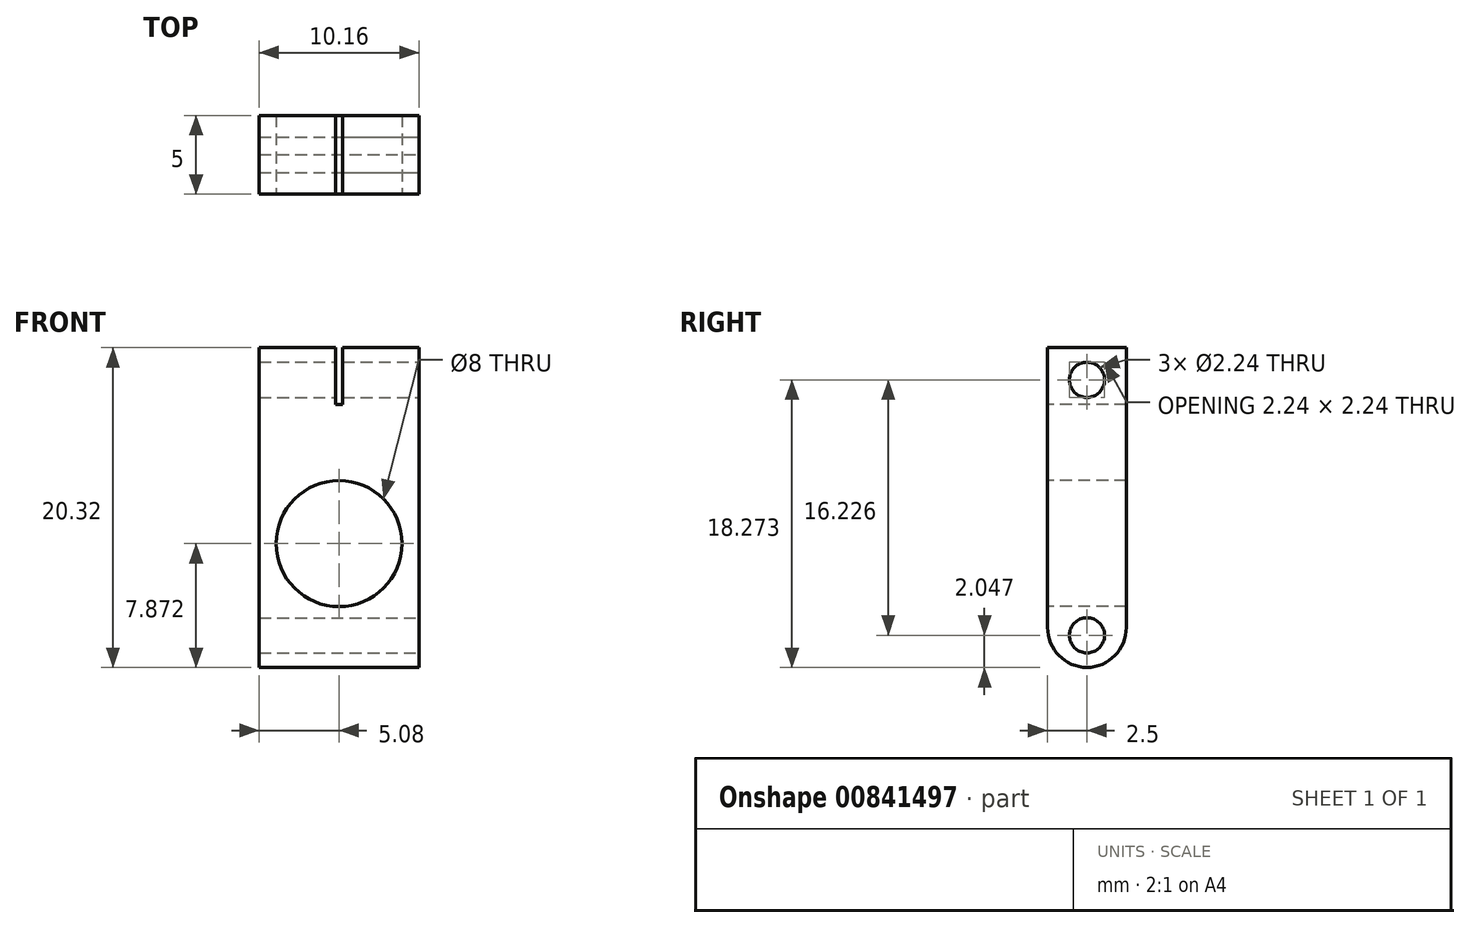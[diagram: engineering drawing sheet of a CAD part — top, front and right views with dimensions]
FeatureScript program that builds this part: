
annotation { "Feature Type Name" : "Feature", "Feature Type Description" : "" }
export const myFeature = defineFeature(function(context is Context, id is Id, definition is map)
    precondition{}
    {
        {
            var Q0;
            Q0=qCreatedBy(makeId("Front.planeOp"),FACE);
            var sketch = newSketch(context, id + "F0", { "sketchPlane" : qUnion([Q0])});
            skLineSegment(sketch, "E0.bottom", {"start": v(5.08, -10.16) * mm, "end": v(-5.08, -10.16) * mm});
            skLineSegment(sketch, "E0.top", {"start": v(5.08, 10.16) * mm, "end": v(-5.08, 10.16) * mm});
            skLineSegment(sketch, "E0.left", {"start": v(5.08, -10.16) * mm, "end": v(5.08, 10.16) * mm});
            skLineSegment(sketch, "E0.right", {"start": v(-5.08, -10.16) * mm, "end": v(-5.08, 10.16) * mm});
            skPoint(sketch, "E0.middle", {"position": v(0, 0) * mm});
            skSolve(sketch);
        }
        {
            var Q0;
            Q0=makeQuery(id+"F0.imprint","IMPRINT",FACE,{"disambiguationData":[TD([[makeQuery(id+"F0.imprint","IMPRINT",EDGE,{"derivedFrom":sQuery(id+"F0.wireOp",EDGE,"E0.bottom")}),-1.0]])]});
            var sketch = newSketch(context, id + "F1", { "sketchPlane" : qUnion([Q0])});
            skCircle(sketch, "E1", {"center": v(0, -2.29) * mm, "radius": 4 * mm});
            skSolve(sketch);
        }
        {
            var Q0;
            Q0 = qSketchRegion(id + "F0", true);
            extrude(context, id + "F2", {"entities" : qUnion([Q0]), "endBound" : BoundingType.SYMMETRIC, "depth" : 5 * mm, "offsetDistance" : 25.4 * mm});
        }
        {
            var Q0;
            Q0 = qSketchRegion(id + "F1", true);
            extrude(context, id + "F3", {"entities" : qUnion([Q0]), "operationType" : NewBodyOperationType.REMOVE, "endBound" : BoundingType.SYMMETRIC, "oppositeDirection" : true, "depth" : 8 * mm, "offsetDistance" : 25.4 * mm});
        }
        {
            var Q0;
            Q0=makeQuery(id+"F2.opExtrude","SWEPT_FACE",FACE,{"disambiguationData":[OSD([sQuery(id+"F0.wireOp",EDGE,"E0.left")])]});
            var sketch = newSketch(context, id + "F4", { "sketchPlane" : qUnion([Q0])});
            skCircle(sketch, "E2", {"center": v(0, -8.11) * mm, "radius": 1.12 * mm});
            skSolve(sketch);
        }
        {
            var Q0;
            Q0 = qSketchRegion(id + "F4", true);
            extrude(context, id + "F5", {"entities" : qUnion([Q0]), "operationType" : NewBodyOperationType.REMOVE, "oppositeDirection" : true, "depth" : 10.16 * mm, "offsetDistance" : 25.4 * mm});
        }
        {
            var Q0;
            Q0=makeQuery(id+"F2.opExtrude","SWEPT_FACE",FACE,{"disambiguationData":[OSD([sQuery(id+"F0.wireOp",EDGE,"E0.top")])]});
            var sketch = newSketch(context, id + "F6", { "sketchPlane" : qUnion([Q0])});
            skLineSegment(sketch, "E3.bottom", {"start": v(-0.23, 2.5) * mm, "end": v(0.23, 2.5) * mm});
            skLineSegment(sketch, "E3.top", {"start": v(-0.23, -2.5) * mm, "end": v(0.23, -2.5) * mm});
            skLineSegment(sketch, "E3.left", {"start": v(-0.23, 2.5) * mm, "end": v(-0.23, -2.5) * mm});
            skLineSegment(sketch, "E3.right", {"start": v(0.23, 2.5) * mm, "end": v(0.23, -2.5) * mm});
            skSolve(sketch);
        }
        {
            var Q0;
            Q0 = qSketchRegion(id + "F6", true);
            extrude(context, id + "F7", {"entities" : qUnion([Q0]), "operationType" : NewBodyOperationType.REMOVE, "oppositeDirection" : true, "depth" : 3.6 * mm, "offsetDistance" : 25.4 * mm});
        }
        {
            var Q0;
            Q0=makeQuery(id+"F2.opExtrude","SWEPT_FACE",FACE,{"disambiguationData":[OSD([sQuery(id+"F0.wireOp",EDGE,"E0.left")])]});
            var sketch = newSketch(context, id + "F8", { "sketchPlane" : qUnion([Q0])});
            skCircle(sketch, "E4", {"center": v(0, 8.11) * mm, "radius": 1.12 * mm});
            skSolve(sketch);
        }
        {
            var Q0;
            Q0 = qSketchRegion(id + "F8", true);
            extrude(context, id + "F9", {"entities" : qUnion([Q0]), "operationType" : NewBodyOperationType.REMOVE, "oppositeDirection" : true, "depth" : 10.16 * mm, "offsetDistance" : 25.4 * mm});
        }
        {
            var Q0;
            Q0=makeQuery(id+"F2.opExtrude","CAP_EDGE",EDGE,{"disambiguationData":[OSD([sQuery(id+"F0.wireOp",EDGE,"E0.bottom")])],"isStart":true});
            var Q1;
            Q1=makeQuery(id+"F2.opExtrude","CAP_EDGE",EDGE,{"disambiguationData":[OSD([sQuery(id+"F0.wireOp",EDGE,"E0.bottom")])],"isStart":false});
            fillet(context, id + "F10", {"entities" : qUnion([Q0, Q1]), "radius" : 2.54 * mm, "tangentPropagation" : true, "allowEdgeOverflow" : false});
        }
    });
